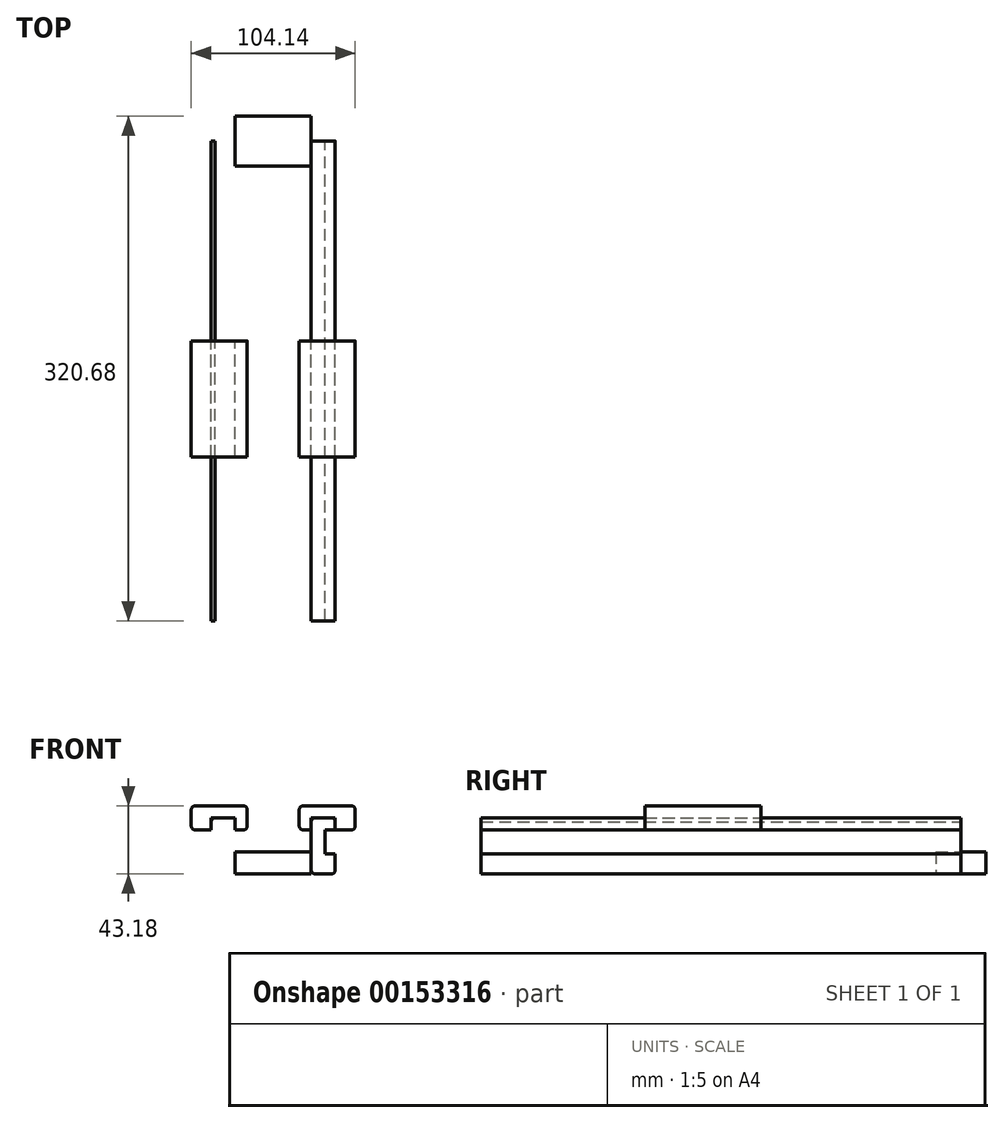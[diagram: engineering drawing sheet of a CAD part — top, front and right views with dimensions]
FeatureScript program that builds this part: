
annotation { "Feature Type Name" : "Feature", "Feature Type Description" : "" }
export const myFeature = defineFeature(function(context is Context, id is Id, definition is map)
    precondition{}
    {
        {
            var Q0;
            Q0=qCreatedBy(makeId("Front.planeOp"),FACE);
            var sketch = newSketch(context, id + "F0", { "sketchPlane" : qUnion([Q0])});
            skLineSegment(sketch, "E0", {"start": v(24.13, 2.54) * mm, "end": v(24.13, 33.02) * mm});
            skLineSegment(sketch, "E1", {"start": v(26.67, 35.56) * mm, "end": v(36.83, 35.56) * mm});
            skLineSegment(sketch, "E2", {"start": v(39.37, 33.02) * mm, "end": v(39.37, 27.94) * mm});
            skLineSegment(sketch, "E3", {"start": v(39.37, 27.94) * mm, "end": v(33.02, 27.94) * mm});
            skLineSegment(sketch, "E4", {"start": v(26.67, 0) * mm, "end": v(36.83, 0) * mm});
            skLineSegment(sketch, "E5", {"start": v(39.37, 2.54) * mm, "end": v(39.37, 12.7) * mm});
            skLineSegment(sketch, "E6", {"start": v(39.37, 12.7) * mm, "end": v(33.02, 12.7) * mm});
            skLineSegment(sketch, "E7", {"start": v(33.02, 12.7) * mm, "end": v(33.02, 27.94) * mm});
            skLineSegment(sketch, "E8", {"start": v(19.05, 43.18) * mm, "end": v(49.53, 43.18) * mm});
            skLineSegment(sketch, "E9", {"start": v(52.07, 40.64) * mm, "end": v(52.07, 30.48) * mm});
            skLineSegment(sketch, "E10", {"start": v(49.53, 27.94) * mm, "end": v(39.37, 27.94) * mm});
            skLineSegment(sketch, "E11", {"start": v(24.13, 27.94) * mm, "end": v(19.05, 27.94) * mm});
            skLineSegment(sketch, "E12", {"start": v(16.5, 30.48) * mm, "end": v(16.5, 40.64) * mm});
            skPoint(sketch, "E13.visualSharp", {"position": v(24.13, 35.56) * mm});
            skArc(sketch, "E13.filletArc", {"start": v(26.67, 35.56) * mm, "mid": v(24.87, 34.82) * mm, "end": v(24.13, 33.02) * mm});
            skLineSegment(sketch, "E14", {"start": v(24.13, 33.02) * mm, "end": v(24.13, 35.56) * mm});
            skLineSegment(sketch, "E15", {"start": v(26.67, 35.56) * mm, "end": v(24.13, 35.56) * mm});
            skPoint(sketch, "E16.visualSharp", {"position": v(39.37, 35.56) * mm});
            skArc(sketch, "E16.filletArc", {"start": v(39.37, 33.02) * mm, "mid": v(38.63, 34.82) * mm, "end": v(36.83, 35.56) * mm});
            skLineSegment(sketch, "E17", {"start": v(36.83, 35.56) * mm, "end": v(39.37, 35.56) * mm});
            skLineSegment(sketch, "E18", {"start": v(39.37, 33.02) * mm, "end": v(39.37, 35.56) * mm});
            skPoint(sketch, "E19.visualSharp", {"position": v(16.5, 43.18) * mm});
            skArc(sketch, "E19.filletArc", {"start": v(19.05, 43.18) * mm, "mid": v(17.25, 42.44) * mm, "end": v(16.5, 40.64) * mm});
            skPoint(sketch, "E20.visualSharp", {"position": v(16.5, 27.94) * mm});
            skArc(sketch, "E20.filletArc", {"start": v(16.5, 30.48) * mm, "mid": v(17.25, 28.68) * mm, "end": v(19.05, 27.94) * mm});
            skPoint(sketch, "E21.visualSharp", {"position": v(52.07, 43.18) * mm});
            skArc(sketch, "E21.filletArc", {"start": v(52.07, 40.64) * mm, "mid": v(51.33, 42.44) * mm, "end": v(49.53, 43.18) * mm});
            skArc(sketch, "E22.filletArc", {"start": v(49.53, 27.94) * mm, "mid": v(51.33, 28.68) * mm, "end": v(52.07, 30.48) * mm});
            skPoint(sketch, "E23.visualSharp", {"position": v(24.13, 0) * mm});
            skArc(sketch, "E23.filletArc", {"start": v(24.13, 2.54) * mm, "mid": v(24.87, 0.74) * mm, "end": v(26.67, 0) * mm});
            skPoint(sketch, "E24.visualSharp", {"position": v(39.37, 0) * mm});
            skArc(sketch, "E24.filletArc", {"start": v(36.83, 0) * mm, "mid": v(38.63, 0.74) * mm, "end": v(39.37, 2.54) * mm});
            skArc(sketch, "E25.MirrorCS", {"start": v(-39.37, 33.02) * mm, "mid": v(-38.63, 34.82) * mm, "end": v(-36.83, 35.56) * mm});
            skLineSegment(sketch, "E26.MirrorCS", {"start": v(-39.37, 33.02) * mm, "end": v(-39.37, 35.56) * mm});
            skLineSegment(sketch, "E27.MirrorCS", {"start": v(-26.67, 35.56) * mm, "end": v(-24.13, 35.56) * mm});
            skLineSegment(sketch, "E28.MirrorCS", {"start": v(-24.13, 33.02) * mm, "end": v(-24.13, 35.56) * mm});
            skLineSegment(sketch, "E29.MirrorCS", {"start": v(-36.83, 35.56) * mm, "end": v(-39.37, 35.56) * mm});
            skArc(sketch, "E30.MirrorCS", {"start": v(-26.67, 35.56) * mm, "mid": v(-24.87, 34.82) * mm, "end": v(-24.13, 33.02) * mm});
            skArc(sketch, "E31.MirrorCS", {"start": v(-49.53, 27.94) * mm, "mid": v(-51.33, 28.68) * mm, "end": v(-52.07, 30.48) * mm});
            skArc(sketch, "E32.MirrorCS", {"start": v(-19.05, 43.18) * mm, "mid": v(-17.25, 42.44) * mm, "end": v(-16.5, 40.64) * mm});
            skArc(sketch, "E33.MirrorCS", {"start": v(-52.07, 40.64) * mm, "mid": v(-51.33, 42.44) * mm, "end": v(-49.53, 43.18) * mm});
            skArc(sketch, "E34.MirrorCS", {"start": v(-16.5, 30.48) * mm, "mid": v(-17.25, 28.68) * mm, "end": v(-19.05, 27.94) * mm});
            skArc(sketch, "E35.MirrorCS", {"start": v(-24.13, 2.54) * mm, "mid": v(-24.87, 0.74) * mm, "end": v(-26.67, 0) * mm});
            skArc(sketch, "E36.MirrorCS", {"start": v(-36.83, 0) * mm, "mid": v(-38.63, 0.74) * mm, "end": v(-39.37, 2.54) * mm});
            skLineSegment(sketch, "E37.MirrorCS", {"start": v(-16.5, 30.48) * mm, "end": v(-16.5, 40.64) * mm});
            skLineSegment(sketch, "E38.MirrorCS", {"start": v(-24.13, 27.94) * mm, "end": v(-19.05, 27.94) * mm});
            skLineSegment(sketch, "E39.MirrorCS", {"start": v(-49.53, 27.94) * mm, "end": v(-39.37, 27.94) * mm});
            skLineSegment(sketch, "E40.MirrorCS", {"start": v(-52.07, 40.64) * mm, "end": v(-52.07, 30.48) * mm});
            skLineSegment(sketch, "E41.MirrorCS", {"start": v(-19.05, 43.18) * mm, "end": v(-49.53, 43.18) * mm});
            skLineSegment(sketch, "E42.MirrorCS", {"start": v(-33.02, 12.7) * mm, "end": v(-33.02, 27.94) * mm});
            skLineSegment(sketch, "E43.MirrorCS", {"start": v(-39.37, 12.7) * mm, "end": v(-33.02, 12.7) * mm});
            skLineSegment(sketch, "E44.MirrorCS", {"start": v(-39.37, 2.54) * mm, "end": v(-39.37, 12.7) * mm});
            skLineSegment(sketch, "E45.MirrorCS", {"start": v(-26.67, 0) * mm, "end": v(-36.83, 0) * mm});
            skPoint(sketch, "E46.MirrorP", {"position": v(-24.13, 35.56) * mm});
            skLineSegment(sketch, "E47.MirrorCS", {"start": v(-39.37, 27.94) * mm, "end": v(-33.02, 27.94) * mm});
            skLineSegment(sketch, "E48.MirrorCS", {"start": v(-39.37, 33.02) * mm, "end": v(-39.37, 27.94) * mm});
            skPoint(sketch, "E49.MirrorP", {"position": v(-39.37, 35.56) * mm});
            skPoint(sketch, "E50.MirrorP", {"position": v(-24.13, 0) * mm});
            skLineSegment(sketch, "E51.MirrorCS", {"start": v(-26.67, 35.56) * mm, "end": v(-36.83, 35.56) * mm});
            skLineSegment(sketch, "E52.MirrorCS", {"start": v(-24.13, 2.54) * mm, "end": v(-24.13, 33.02) * mm});
            skPoint(sketch, "E53.MirrorP", {"position": v(-16.5, 43.18) * mm});
            skPoint(sketch, "E54.MirrorP", {"position": v(-39.37, 0) * mm});
            skPoint(sketch, "E55.MirrorP", {"position": v(-16.5, 27.94) * mm});
            skPoint(sketch, "E56.MirrorP", {"position": v(-52.07, 43.18) * mm});
            skLineSegment(sketch, "E57.bottom", {"start": v(-24.13, 13.97) * mm, "end": v(24.13, 13.97) * mm});
            skLineSegment(sketch, "E57.top", {"start": v(-24.13, 0) * mm, "end": v(24.13, 0) * mm});
            skLineSegment(sketch, "E57.left", {"start": v(-24.13, 13.97) * mm, "end": v(-24.13, 0) * mm});
            skLineSegment(sketch, "E57.right", {"start": v(24.13, 13.97) * mm, "end": v(24.13, 0) * mm});
            skSolve(sketch);
        }
        {
            var Q0;
            Q0=makeQuery(id+"F0.imprint","IMPRINT",FACE,{"disambiguationData":[TD([[makeQuery(id+"F0.imprint","IMPRINT",EDGE,{"derivedFrom":sQuery(id+"F0.wireOp",EDGE,"E25.MirrorCS")}),-1.0]])]});
            var Q1;
            Q1=makeQuery(id+"F0.imprint","IMPRINT",FACE,{"disambiguationData":[TD([[makeQuery(id+"F0.imprint","IMPRINT",EDGE,{"derivedFrom":sQuery(id+"F0.wireOp",EDGE,"E1")}),-1.0]])]});
            extrude(context, id + "F1", {"entities" : qUnion([Q0, Q1]), "depth" : 304.8 * mm});
        }
        {
            var Q0;
            Q0=makeQuery(id+"F0.imprint","IMPRINT",FACE,{"disambiguationData":[TD([[makeQuery(id+"F0.imprint","IMPRINT",EDGE,{"derivedFrom":sQuery(id+"F0.wireOp",EDGE,"E26.MirrorCS")}),1.0]])]});
            var Q1;
            Q1=makeQuery(id+"F0.imprint","IMPRINT",FACE,{"disambiguationData":[TD([[makeQuery(id+"F0.imprint","IMPRINT",EDGE,{"derivedFrom":sQuery(id+"F0.wireOp",EDGE,"E1")}),1.0]])]});
            extrude(context, id + "F2", {"entities" : qUnion([Q0, Q1]), "depth" : 200.66 * mm, "hasSecondDirection" : true, "secondDirectionOppositeDirection" : false, "secondDirectionDepth" : 127 * mm});
        }
        {
            var Q0;
            Q0=qCreatedBy(makeId("Front.planeOp"),FACE);
            var sketch = newSketch(context, id + "F3", { "sketchPlane" : qUnion([Q0])});
            skCircle(sketch, "E58", {"center": v(0, 35.56) * mm, "radius": 24 * mm});
            skCircle(sketch, "E59", {"center": v(0, 35.56) * mm, "radius": 14 * mm});
            skCircle(sketch, "E60", {"center": v(0, 35.56) * mm, "radius": 6 * mm});
            skCircle(sketch, "E61", {"center": v(0, 35.56) * mm, "radius": 19 * mm, "construction": true});
            skLineSegment(sketch, "E62", {"start": v(-13.27, 55.56) * mm, "end": v(13.27, 55.56) * mm});
            skLineSegment(sketch, "E63", {"start": v(-13.27, 15.56) * mm, "end": v(13.27, 15.56) * mm});
            skCircle(sketch, "E64", {"center": v(-19, 35.56) * mm, "radius": 3.42 * mm});
            skCircle(sketch, "E65.1.0", {"center": v(-13.44, 22.12) * mm, "radius": 3.42 * mm});
            skCircle(sketch, "E65.3.0", {"center": v(13.44, 22.12) * mm, "radius": 3.42 * mm});
            skCircle(sketch, "E65.4.0", {"center": v(19, 35.56) * mm, "radius": 3.42 * mm});
            skCircle(sketch, "E65.5.0", {"center": v(13.44, 49) * mm, "radius": 3.42 * mm});
            skCircle(sketch, "E65.7.0", {"center": v(-13.44, 49) * mm, "radius": 3.42 * mm});
            skSolve(sketch);
        }
        {
            var Q0;
            {var subQ3=sQuery(id+"F0.wireOp",EDGE,"E57.bottom");Q0=makeQuery(id+"F0.imprint","IMPRINT",FACE,{"disambiguationData":[TD([[makeQuery(id+"F0.imprint","IMPRINT",EDGE,{"derivedFrom":subQ3}),-1.0]])]});}
            extrude(context, id + "F4", {"entities" : qUnion([Q0]), "depth" : 15.88 * mm, "hasSecondDirection" : true, "secondDirectionOppositeDirection" : true, "secondDirectionDepth" : 15.88 * mm});
        }
    });
